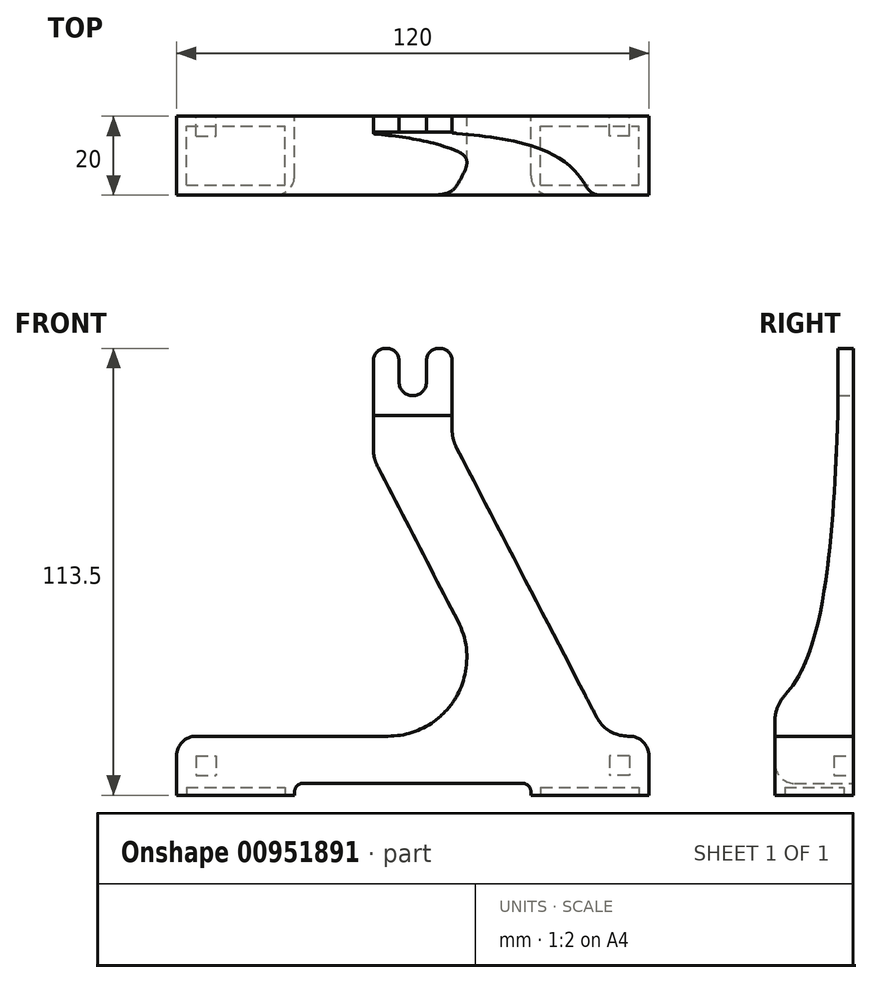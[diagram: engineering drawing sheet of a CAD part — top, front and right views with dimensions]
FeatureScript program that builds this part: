
annotation { "Feature Type Name" : "Feature", "Feature Type Description" : "" }
export const myFeature = defineFeature(function(context is Context, id is Id, definition is map)
    precondition{}
    {
        {
            var Q0;
            Q0=qCreatedBy(makeId("Front.planeOp"),FACE);
            var sketch = newSketch(context, id + "F0", { "sketchPlane" : qUnion([Q0])});
            skArc(sketch, "E0", {"start": v(-3.5, 105) * mm, "mid": v(0, 101.5) * mm, "end": v(3.5, 105) * mm});
            skCircle(sketch, "E1", {"center": v(0, 105) * mm, "radius": 100 * mm, "construction": true});
            skLineSegment(sketch, "E2", {"start": v(-10, 110.5) * mm, "end": v(-10, 87.96) * mm});
            skLineSegment(sketch, "E3", {"start": v(-20, 15) * mm, "end": v(-55, 15) * mm});
            skLineSegment(sketch, "E4", {"start": v(-60, 10) * mm, "end": v(-60, 0) * mm});
            skLineSegment(sketch, "E5", {"start": v(-60, 0) * mm, "end": v(-30, 0) * mm});
            skLineSegment(sketch, "E6", {"start": v(-28, 3) * mm, "end": v(28, 3) * mm});
            skLineSegment(sketch, "E7", {"start": v(30, 0) * mm, "end": v(60, 0) * mm});
            skLineSegment(sketch, "E8", {"start": v(60, 0) * mm, "end": v(60, 10) * mm});
            skLineSegment(sketch, "E9", {"start": v(55, 15) * mm, "end": v(54.7, 15) * mm});
            skLineSegment(sketch, "E10", {"start": v(10, 92.85) * mm, "end": v(10, 110.5) * mm});
            skLineSegment(sketch, "E11", {"start": v(7, 113.5) * mm, "end": v(6.5, 113.5) * mm});
            skLineSegment(sketch, "E12", {"start": v(-30, 1) * mm, "end": v(-30, 0) * mm});
            skLineSegment(sketch, "E13", {"start": v(30, 1) * mm, "end": v(30, 0) * mm});
            skPoint(sketch, "E14.orphan", {"position": v(-45, 0) * mm});
            skPoint(sketch, "E15.orphan", {"position": v(45, 0) * mm});
            skPoint(sketch, "E16.visualSharp", {"position": v(-10, 15) * mm});
            skPoint(sketch, "E17.visualSharp", {"position": v(10, 15) * mm});
            skPoint(sketch, "E18.visualSharp", {"position": v(-10, 113.5) * mm});
            skArc(sketch, "E18.filletArc", {"start": v(-7, 113.5) * mm, "mid": v(-9.12, 112.62) * mm, "end": v(-10, 110.5) * mm});
            skPoint(sketch, "E19.visualSharp", {"position": v(10, 113.5) * mm});
            skArc(sketch, "E19.filletArc", {"start": v(10, 110.5) * mm, "mid": v(9.12, 112.62) * mm, "end": v(7, 113.5) * mm});
            skPoint(sketch, "E20.visualSharp", {"position": v(-60, 15) * mm});
            skArc(sketch, "E20.filletArc", {"start": v(-55, 15) * mm, "mid": v(-58.54, 13.54) * mm, "end": v(-60, 10) * mm});
            skPoint(sketch, "E21.visualSharp", {"position": v(60, 15) * mm});
            skArc(sketch, "E21.filletArc", {"start": v(60, 10) * mm, "mid": v(58.54, 13.54) * mm, "end": v(55, 15) * mm});
            skPoint(sketch, "E22.visualSharp", {"position": v(30, 3) * mm});
            skArc(sketch, "E22.filletArc", {"start": v(30, 1) * mm, "mid": v(29.41, 2.41) * mm, "end": v(28, 3) * mm});
            skPoint(sketch, "E23.visualSharp", {"position": v(-30, 3) * mm});
            skArc(sketch, "E23.filletArc", {"start": v(-28, 3) * mm, "mid": v(-29.41, 2.41) * mm, "end": v(-30, 1) * mm});
            skLineSegment(sketch, "E24", {"start": v(-3.5, 105) * mm, "end": v(-3.5, 110.5) * mm});
            skLineSegment(sketch, "E25", {"start": v(3.5, 105) * mm, "end": v(3.5, 110.5) * mm});
            skLineSegment(sketch, "E26.trimOffspring", {"start": v(-6.5, 113.5) * mm, "end": v(-7, 113.5) * mm});
            skPoint(sketch, "E27.visualSharp", {"position": v(-3.5, 113.5) * mm});
            skArc(sketch, "E27.filletArc", {"start": v(-3.5, 110.5) * mm, "mid": v(-4.38, 112.62) * mm, "end": v(-6.5, 113.5) * mm});
            skPoint(sketch, "E28.visualSharp", {"position": v(3.5, 113.5) * mm});
            skArc(sketch, "E28.filletArc", {"start": v(6.5, 113.5) * mm, "mid": v(4.38, 112.62) * mm, "end": v(3.5, 110.5) * mm});
            skLineSegment(sketch, "E29", {"start": v(11.13, 88.23) * mm, "end": v(46.72, 19.85) * mm});
            skLineSegment(sketch, "E30", {"start": v(-8.87, 83.34) * mm, "end": v(11.48, 44.23) * mm});
            skLineSegment(sketch, "E31.trimOffspring", {"start": v(-6.26, 15) * mm, "end": v(-20, 15) * mm});
            skPoint(sketch, "E32.visualSharp", {"position": v(-10, 85.5) * mm});
            skArc(sketch, "E32.filletArc", {"start": v(-10, 87.96) * mm, "mid": v(-9.71, 85.58) * mm, "end": v(-8.87, 83.34) * mm});
            skPoint(sketch, "E33.visualSharp", {"position": v(10, 90.4) * mm});
            skArc(sketch, "E33.filletArc", {"start": v(10, 92.85) * mm, "mid": v(10.29, 90.47) * mm, "end": v(11.13, 88.23) * mm});
            skPoint(sketch, "E34.visualSharp", {"position": v(49.24, 15) * mm});
            skArc(sketch, "E34.filletArc", {"start": v(46.72, 19.85) * mm, "mid": v(50.03, 16.3) * mm, "end": v(54.7, 15) * mm});
            skPoint(sketch, "E35.visualSharp", {"position": v(26.7, 15) * mm});
            skArc(sketch, "E35.filletArc", {"start": v(-6.26, 15) * mm, "mid": v(10.84, 24.62) * mm, "end": v(11.48, 44.23) * mm});
            skSolve(sketch);
        }
        {
            var Q0;
            Q0=makeQuery(id+"F0.imprint","IMPRINT",FACE,{"disambiguationData":[TD([[makeQuery(id+"F0.imprint","IMPRINT",EDGE,{"derivedFrom":sQuery(id+"F0.wireOp",EDGE,"E0")}),-1.0]])]});
            extrude(context, id + "F1", {"entities" : qUnion([Q0]), "depth" : 20 * mm, "offsetDistance" : 25 * mm});
        }
        {
            var Q0;
            Q0=makeQuery(id+"F1.opExtrude","SWEPT_FACE",FACE,{"disambiguationData":[OSD([sQuery(id+"F0.wireOp",EDGE,"E10")])]});
            var sketch = newSketch(context, id + "F2", { "sketchPlane" : qUnion([Q0])});
            skLineSegment(sketch, "E36", {"start": v(-4, 116.6) * mm, "end": v(-4, 96.5) * mm});
            skLineSegment(sketch, "E37", {"start": v(-20, 116.6) * mm, "end": v(-4, 116.6) * mm});
            skPoint(sketch, "E38.visualSharp", {"position": v(-4, 88.5) * mm});
            skLineSegment(sketch, "E39", {"start": v(-25.17, 79.44) * mm, "end": v(-25.17, 116.6) * mm});
            skLineSegment(sketch, "E40", {"start": v(-25.17, 116.6) * mm, "end": v(-20, 116.6) * mm});
            skPoint(sketch, "E41.visualSharp", {"position": v(-20, 88.5) * mm});
            skFitSpline(sketch, "E42", {"points": [v(-4, 96.5) * mm, v(-13.32, 31.43) * mm, v(-22.33, 23.5) * mm, v(-25.17, 79.44) * mm], "startDerivative": vector(-7.01, -189.31) * mm, "endDerivative": vector(0.02, 210.5) * mm});
            skSolve(sketch);
        }
        {
            var Q0;
            Q0=makeQuery(id+"F1.opExtrude","SWEPT_FACE",FACE,{"disambiguationData":[OSD([sQuery(id+"F0.wireOp",EDGE,"E5")])]});
            var sketch = newSketch(context, id + "F3", { "sketchPlane" : qUnion([Q0])});
            skLineSegment(sketch, "E43.bottom", {"start": v(-57.5, 17.5) * mm, "end": v(-32.5, 17.5) * mm});
            skLineSegment(sketch, "E43.top", {"start": v(-57.5, 2.5) * mm, "end": v(-32.5, 2.5) * mm});
            skLineSegment(sketch, "E43.left", {"start": v(-57.5, 17.5) * mm, "end": v(-57.5, 2.5) * mm});
            skLineSegment(sketch, "E43.right", {"start": v(-32.5, 17.5) * mm, "end": v(-32.5, 2.5) * mm});
            skLineSegment(sketch, "E44.bottom", {"start": v(32.5, 17.5) * mm, "end": v(57.5, 17.5) * mm});
            skLineSegment(sketch, "E44.top", {"start": v(32.5, 2.5) * mm, "end": v(57.5, 2.5) * mm});
            skLineSegment(sketch, "E44.left", {"start": v(32.5, 17.5) * mm, "end": v(32.5, 2.5) * mm});
            skLineSegment(sketch, "E44.right", {"start": v(57.5, 17.5) * mm, "end": v(57.5, 2.5) * mm});
            skSolve(sketch);
        }
        {
            var Q0;
            Q0=makeQuery(id+"F3.imprint","IMPRINT",FACE,{"disambiguationData":[TD([[makeQuery(id+"F3.imprint","IMPRINT",EDGE,{"derivedFrom":sQuery(id+"F3.wireOp",EDGE,"E43.bottom")}),-1.0]])]});
            var Q1;
            Q1=makeQuery(id+"F3.imprint","IMPRINT",FACE,{"disambiguationData":[TD([[makeQuery(id+"F3.imprint","IMPRINT",EDGE,{"derivedFrom":sQuery(id+"F3.wireOp",EDGE,"E44.bottom")}),-1.0]])]});
            extrude(context, id + "F4", {"entities" : qUnion([Q0, Q1]), "operationType" : NewBodyOperationType.REMOVE, "oppositeDirection" : true, "depth" : 2 * mm, "offsetDistance" : 25 * mm});
        }
        {
            var Q0;
            {var subQ1=sQuery(id+"F2.wireOp",EDGE,"E37");Q0=makeQuery(id+"F2.imprint","IMPRINT",FACE,{"disambiguationData":[TD([[makeQuery(id+"F2.imprint","IMPRINT",EDGE,{"derivedFrom":subQ1}),-1.0]])]});}
            var Q1;
            {var subQ0=sQuery(id+"F0.wireOp",EDGE,"E10");var subQ1=makeQuery(id+"F1.opExtrude","CAP_EDGE",EDGE,{"disambiguationData":[OSD([subQ0])],"isStart":false});Q1=makeQuery(id+"F2.imprint","IMPRINT",FACE,{"disambiguationData":[TD([[makeQuery(id+"F2.imprint","IMPRINT",EDGE,{"derivedFrom":subQ1}),-1.0]])]});}
            extrude(context, id + "F5", {"entities" : qUnion([Q0, Q1]), "operationType" : NewBodyOperationType.REMOVE, "depth" : 75 * mm, "offsetDistance" : 25 * mm, "symmetric" : true});
        }
        {
            var Q0;
            Q0=makeQuery(id+"F5.boolean.opBoolean","INTERSECT",EDGE,{"derivedFrom":[makeQuery(id+"F1.opExtrude","CAP_FACE",FACE,{"disambiguationData":[OSD([sQuery(id+"F0.wireOp",EDGE,"E0"),sQuery(id+"F0.wireOp",EDGE,"E2"),sQuery(id+"F0.wireOp",EDGE,"E3"),sQuery(id+"F0.wireOp",EDGE,"E4"),sQuery(id+"F0.wireOp",EDGE,"E5"),sQuery(id+"F0.wireOp",EDGE,"E6"),sQuery(id+"F0.wireOp",EDGE,"E7"),sQuery(id+"F0.wireOp",EDGE,"E8"),sQuery(id+"F0.wireOp",EDGE,"E9"),sQuery(id+"F0.wireOp",EDGE,"E10"),sQuery(id+"F0.wireOp",EDGE,"E11"),sQuery(id+"F0.wireOp",EDGE,"E12"),sQuery(id+"F0.wireOp",EDGE,"E13"),sQuery(id+"F0.wireOp",EDGE,"E18.filletArc"),sQuery(id+"F0.wireOp",EDGE,"E19.filletArc"),sQuery(id+"F0.wireOp",EDGE,"E20.filletArc"),sQuery(id+"F0.wireOp",EDGE,"E21.filletArc"),sQuery(id+"F0.wireOp",EDGE,"E22.filletArc"),sQuery(id+"F0.wireOp",EDGE,"E23.filletArc"),sQuery(id+"F0.wireOp",EDGE,"E24"),sQuery(id+"F0.wireOp",EDGE,"E25"),sQuery(id+"F0.wireOp",EDGE,"E26.trimOffspring"),sQuery(id+"F0.wireOp",EDGE,"E27.filletArc"),sQuery(id+"F0.wireOp",EDGE,"E28.filletArc"),sQuery(id+"F0.wireOp",EDGE,"E29"),sQuery(id+"F0.wireOp",EDGE,"E30"),sQuery(id+"F0.wireOp",EDGE,"E31.trimOffspring"),sQuery(id+"F0.wireOp",EDGE,"E32.filletArc"),sQuery(id+"F0.wireOp",EDGE,"E33.filletArc"),sQuery(id+"F0.wireOp",EDGE,"E34.filletArc"),sQuery(id+"F0.wireOp",EDGE,"E35.filletArc")])],"isStart":false}),makeQuery(id+"F5.opExtrude","SWEPT_FACE",FACE,{"disambiguationData":[OSD([sQuery(id+"F2.wireOp",EDGE,"E42")])]})]});
            fillet(context, id + "F6", {"entities" : qUnion([Q0]), "radius" : 10 * mm, "tangentPropagation" : true, "allowEdgeOverflow" : false});
        }
        {
            var Q0;
            Q0=makeQuery(id+"F1.opExtrude","CAP_EDGE",EDGE,{"disambiguationData":[OSD([sQuery(id+"F0.wireOp",EDGE,"E6")])],"isStart":false});
            fillet(context, id + "F7", {"entities" : qUnion([Q0]), "radius" : 5 * mm, "tangentPropagation" : true, "allowEdgeOverflow" : false});
        }
        {
            var Q0;
            Q0=makeQuery(id+"F0.imprint","IMPRINT",FACE,{"disambiguationData":[TD([[makeQuery(id+"F0.imprint","IMPRINT",EDGE,{"derivedFrom":sQuery(id+"F0.wireOp",EDGE,"E0")}),-1.0]])]});
            var sketch = newSketch(context, id + "F8", { "sketchPlane" : qUnion([Q0])});
            skLineSegment(sketch, "E45.bottom", {"start": v(55, 10) * mm, "end": v(50, 10) * mm});
            skLineSegment(sketch, "E45.top", {"start": v(55, 5) * mm, "end": v(50, 5) * mm});
            skLineSegment(sketch, "E45.left", {"start": v(55, 10) * mm, "end": v(55, 5) * mm});
            skLineSegment(sketch, "E45.right", {"start": v(50, 10) * mm, "end": v(50, 5) * mm});
            skLineSegment(sketch, "E46.bottom", {"start": v(-55, 10) * mm, "end": v(-50, 10) * mm});
            skLineSegment(sketch, "E46.top", {"start": v(-55, 5) * mm, "end": v(-50, 5) * mm});
            skLineSegment(sketch, "E46.left", {"start": v(-55, 10) * mm, "end": v(-55, 5) * mm});
            skLineSegment(sketch, "E46.right", {"start": v(-50, 10) * mm, "end": v(-50, 5) * mm});
            skSolve(sketch);
        }
        {
            var Q0;
            Q0=makeQuery(id+"F8.imprint","IMPRINT",FACE,{"disambiguationData":[TD([[makeQuery(id+"F8.imprint","IMPRINT",EDGE,{"derivedFrom":sQuery(id+"F8.wireOp",EDGE,"E45.bottom")}),1.0]])]});
            var Q1;
            Q1=makeQuery(id+"F8.imprint","IMPRINT",FACE,{"disambiguationData":[TD([[makeQuery(id+"F8.imprint","IMPRINT",EDGE,{"derivedFrom":sQuery(id+"F8.wireOp",EDGE,"E46.bottom")}),-1.0]])]});
            extrude(context, id + "F9", {"entities" : qUnion([Q0, Q1]), "operationType" : NewBodyOperationType.REMOVE, "depth" : 5 * mm, "offsetDistance" : 25 * mm});
        }
    });
